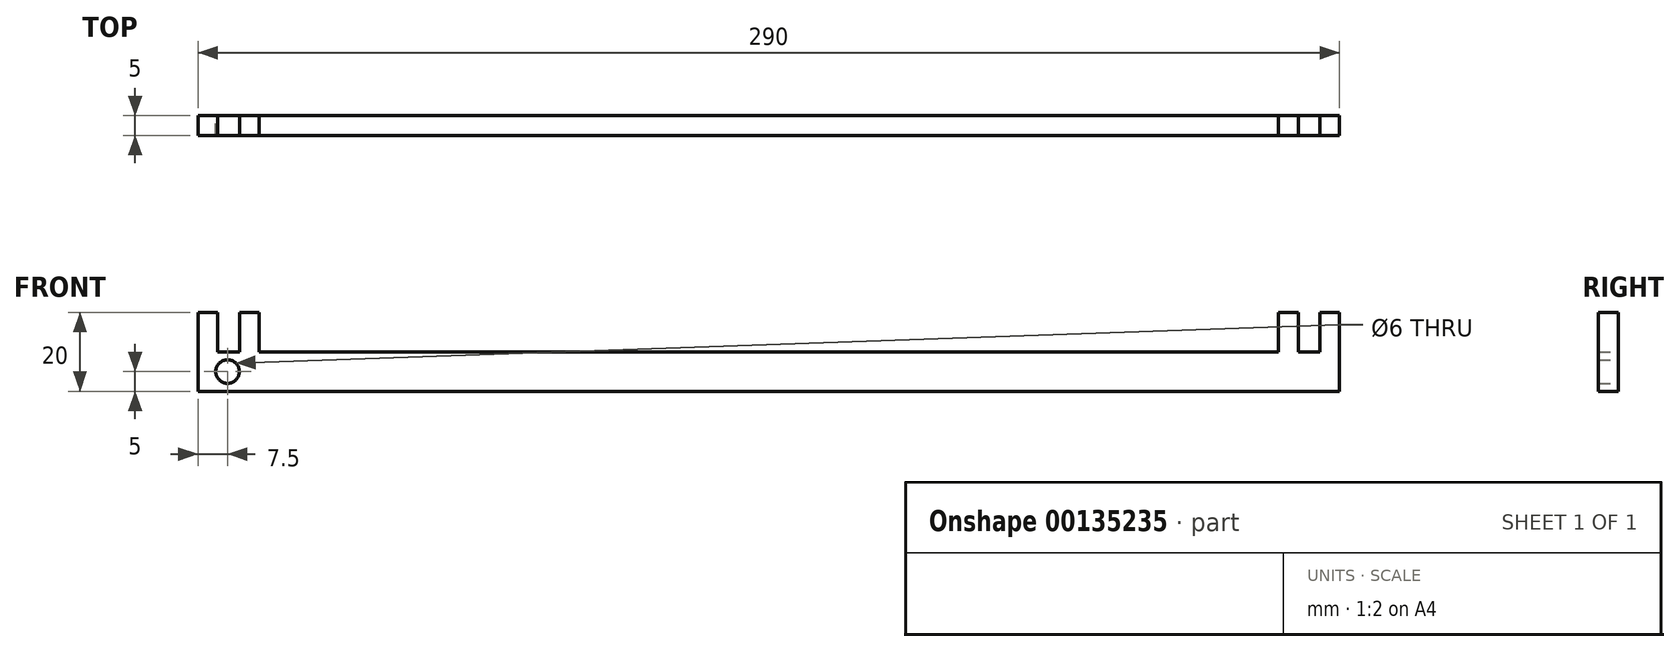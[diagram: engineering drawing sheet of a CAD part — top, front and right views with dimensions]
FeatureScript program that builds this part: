
annotation { "Feature Type Name" : "Feature", "Feature Type Description" : "" }
export const myFeature = defineFeature(function(context is Context, id is Id, definition is map)
    precondition{}
    {
        {
            var Q0;
            Q0=qCreatedBy(makeId("Front.planeOp"),FACE);
            var sketch = newSketch(context, id + "F0", { "sketchPlane" : qUnion([Q0])});
            skLineSegment(sketch, "E0.bottom", {"start": v(145, -10) * mm, "end": v(-145, -10) * mm});
            skLineSegment(sketch, "E0.top", {"start": v(145, 10) * mm, "end": v(140, 10) * mm});
            skLineSegment(sketch, "E0.left", {"start": v(145, -10) * mm, "end": v(145, 10) * mm});
            skLineSegment(sketch, "E0.right", {"start": v(-145, -10) * mm, "end": v(-145, 10) * mm});
            skPoint(sketch, "E0.middle", {"position": v(0, 0) * mm});
            skLineSegment(sketch, "E1", {"start": v(-140, 10) * mm, "end": v(-140, 0) * mm});
            skLineSegment(sketch, "E2", {"start": v(-140, 0) * mm, "end": v(-134.5, 0) * mm});
            skLineSegment(sketch, "E3", {"start": v(140, 0) * mm, "end": v(140, 10) * mm});
            skLineSegment(sketch, "E4.trimOffspring", {"start": v(-140, 10) * mm, "end": v(-145, 10) * mm});
            skLineSegment(sketch, "E5", {"start": v(-134.5, 0) * mm, "end": v(-134.5, 10) * mm});
            skLineSegment(sketch, "E6", {"start": v(-134.5, 10) * mm, "end": v(-129.5, 10) * mm});
            skLineSegment(sketch, "E7", {"start": v(-129.5, 10) * mm, "end": v(-129.5, 0) * mm});
            skLineSegment(sketch, "E8", {"start": v(134.5, 0) * mm, "end": v(134.5, 10) * mm});
            skLineSegment(sketch, "E9", {"start": v(134.5, 10) * mm, "end": v(129.5, 10) * mm});
            skLineSegment(sketch, "E10", {"start": v(129.5, 10) * mm, "end": v(129.5, 0) * mm});
            skLineSegment(sketch, "E11.trimOffspring", {"start": v(134.5, 0) * mm, "end": v(140, 0) * mm});
            skLineSegment(sketch, "E12.trimOffspring", {"start": v(-129.5, 0) * mm, "end": v(129.5, 0) * mm});
            skCircle(sketch, "E13", {"center": v(-137.5, -5) * mm, "radius": 3 * mm});
            skSolve(sketch);
        }
        {
            var Q0;
            Q0=makeQuery(id+"F0.imprint","IMPRINT",FACE,{"disambiguationData":[TD([[makeQuery(id+"F0.imprint","IMPRINT",EDGE,{"derivedFrom":sQuery(id+"F0.wireOp",EDGE,"E0.bottom")}),-1.0]])]});
            extrude(context, id + "F1", {"entities" : qUnion([Q0]), "depth" : 5 * mm});
        }
    });
